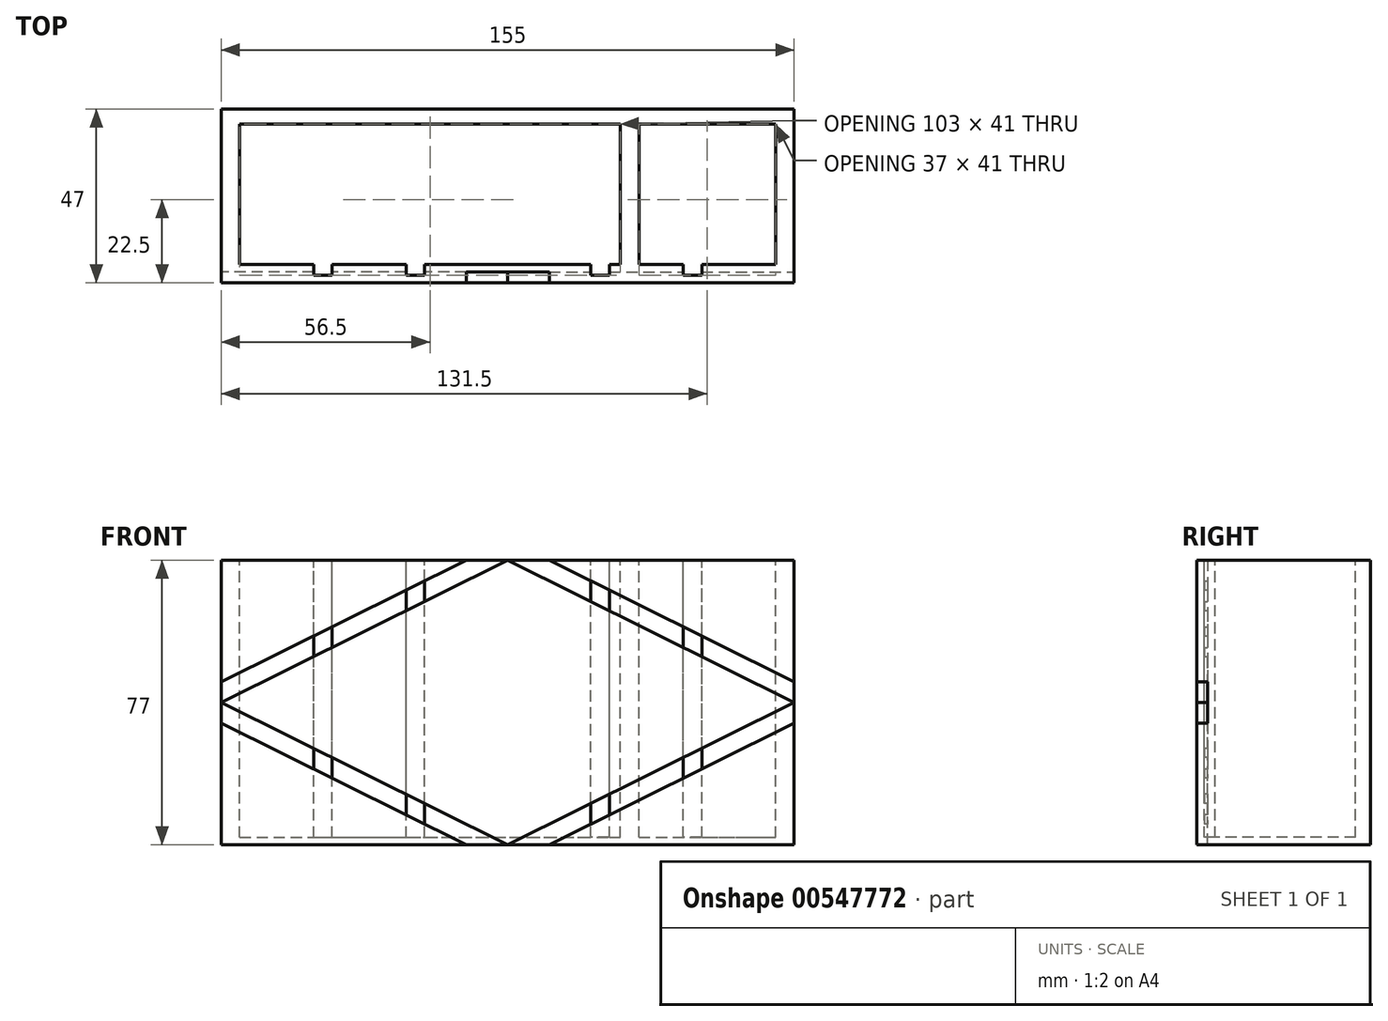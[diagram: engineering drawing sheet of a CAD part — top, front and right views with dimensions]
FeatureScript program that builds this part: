
annotation { "Feature Type Name" : "Feature", "Feature Type Description" : "" }
export const myFeature = defineFeature(function(context is Context, id is Id, definition is map)
    precondition{}
    {
        {
            var Q0;
            Q0=qCreatedBy(makeId("Top.planeOp"),FACE);
            var sketch = newSketch(context, id + "F0", { "sketchPlane" : qUnion([Q0])});
            skLineSegment(sketch, "E0.bottom", {"start": v(-77.5, 23.5) * mm, "end": v(77.5, 23.5) * mm});
            skLineSegment(sketch, "E0.top", {"start": v(-77.5, -23.5) * mm, "end": v(77.5, -23.5) * mm});
            skLineSegment(sketch, "E0.left", {"start": v(-77.5, 23.5) * mm, "end": v(-77.5, -23.5) * mm});
            skLineSegment(sketch, "E0.right", {"start": v(77.5, 23.5) * mm, "end": v(77.5, -23.5) * mm});
            skLineSegment(sketch, "E1", {"start": v(-77.5, 23.5) * mm, "end": v(77.5, -23.5) * mm, "construction": true});
            skSolve(sketch);
        }
        {
            var Q0;
            Q0=makeQuery(id+"F0.imprint","IMPRINT",FACE,{"disambiguationData":[TD([[makeQuery(id+"F0.imprint","IMPRINT",EDGE,{"derivedFrom":sQuery(id+"F0.wireOp",EDGE,"E0.bottom")}),-1.0]])]});
            extrude(context, id + "F1", {"entities" : qUnion([Q0]), "depth" : 77 * mm, "offsetDistance" : 25.4 * mm});
        }
        {
            var Q0;
            Q0=makeQuery(id+"F1.opExtrude","CAP_FACE",FACE,{"disambiguationData":[OSD([sQuery(id+"F0.wireOp",EDGE,"E0.bottom"),sQuery(id+"F0.wireOp",EDGE,"E0.top"),sQuery(id+"F0.wireOp",EDGE,"E0.left"),sQuery(id+"F0.wireOp",EDGE,"E0.right")])],"isStart":false});
            var sketch = newSketch(context, id + "F2", { "sketchPlane" : qUnion([Q0])});
            skLineSegment(sketch, "E2.bottom", {"start": v(-72.5, 19.5) * mm, "end": v(30.5, 19.5) * mm});
            skLineSegment(sketch, "E2.top", {"start": v(-72.5, -18.5) * mm, "end": v(30.5, -18.5) * mm});
            skLineSegment(sketch, "E2.left", {"start": v(-72.5, 19.5) * mm, "end": v(-72.5, -18.5) * mm});
            skLineSegment(sketch, "E2.right", {"start": v(30.5, 19.5) * mm, "end": v(30.5, -18.5) * mm});
            skLineSegment(sketch, "E3.bottom", {"start": v(35.5, 19.5) * mm, "end": v(72.5, 19.5) * mm});
            skLineSegment(sketch, "E3.top", {"start": v(35.5, -18.5) * mm, "end": v(72.5, -18.5) * mm});
            skLineSegment(sketch, "E3.left", {"start": v(35.5, 19.5) * mm, "end": v(35.5, -18.5) * mm});
            skLineSegment(sketch, "E3.right", {"start": v(72.5, 19.5) * mm, "end": v(72.5, -18.5) * mm});
            skSolve(sketch);
        }
        {
            var Q0;
            Q0=makeQuery(id+"F2.imprint","IMPRINT",FACE,{"disambiguationData":[TD([[makeQuery(id+"F2.imprint","IMPRINT",EDGE,{"derivedFrom":sQuery(id+"F2.wireOp",EDGE,"E2.bottom")}),-1.0]])]});
            var Q1;
            Q1=makeQuery(id+"F2.imprint","IMPRINT",FACE,{"disambiguationData":[TD([[makeQuery(id+"F2.imprint","IMPRINT",EDGE,{"derivedFrom":sQuery(id+"F2.wireOp",EDGE,"E3.bottom")}),-1.0]])]});
            extrude(context, id + "F3", {"entities" : qUnion([Q0, Q1]), "operationType" : NewBodyOperationType.REMOVE, "oppositeDirection" : true, "depth" : 75 * mm, "offsetDistance" : 25.4 * mm});
        }
        {
            var Q0;
            Q0=makeQuery(id+"F1.opExtrude","SWEPT_FACE",FACE,{"disambiguationData":[OSD([sQuery(id+"F0.wireOp",EDGE,"E0.top")])]});
            var sketch = newSketch(context, id + "F4", { "sketchPlane" : qUnion([Q0])});
            skLineSegment(sketch, "E4", {"start": v(0, 77) * mm, "end": v(77.5, 38.5) * mm});
            skLineSegment(sketch, "E5", {"start": v(77.5, 38.5) * mm, "end": v(0, 0) * mm});
            skLineSegment(sketch, "E6", {"start": v(0, 0) * mm, "end": v(-77.5, 38.5) * mm});
            skLineSegment(sketch, "E7", {"start": v(-77.5, 38.5) * mm, "end": v(0, 77) * mm});
            skLineSegment(sketch, "E8.0", {"start": v(-88.74, 38.5) * mm, "end": v(0, 82.58) * mm});
            skLineSegment(sketch, "E8.1", {"start": v(0, -5.58) * mm, "end": v(-88.74, 38.5) * mm});
            skLineSegment(sketch, "E8.2", {"start": v(88.74, 38.5) * mm, "end": v(0, -5.58) * mm});
            skLineSegment(sketch, "E8.3", {"start": v(0, 82.58) * mm, "end": v(88.74, 38.5) * mm});
            skSolve(sketch);
        }
        {
            var Q0;
            {var subQ0=sQuery(id+"F4.wireOp",EDGE,"E7");Q0=makeQuery(id+"F4.imprint","IMPRINT",FACE,{"disambiguationData":[TD([[makeQuery(id+"F4.imprint","IMPRINT",EDGE,{"derivedFrom":subQ0}),1.0]])]});}
            var Q1;
            {var subQ0=sQuery(id+"F4.wireOp",EDGE,"E6");Q1=makeQuery(id+"F4.imprint","IMPRINT",FACE,{"disambiguationData":[TD([[makeQuery(id+"F4.imprint","IMPRINT",EDGE,{"derivedFrom":subQ0}),1.0]])]});}
            var Q2;
            {var subQ0=sQuery(id+"F4.wireOp",EDGE,"E5");Q2=makeQuery(id+"F4.imprint","IMPRINT",FACE,{"disambiguationData":[TD([[makeQuery(id+"F4.imprint","IMPRINT",EDGE,{"derivedFrom":subQ0}),1.0]])]});}
            var Q3;
            {var subQ0=sQuery(id+"F4.wireOp",EDGE,"E4");Q3=makeQuery(id+"F4.imprint","IMPRINT",FACE,{"disambiguationData":[TD([[makeQuery(id+"F4.imprint","IMPRINT",EDGE,{"derivedFrom":subQ0}),1.0]])]});}
            extrude(context, id + "F5", {"entities" : qUnion([Q0, Q1, Q2, Q3]), "operationType" : NewBodyOperationType.REMOVE, "oppositeDirection" : true, "depth" : 3 * mm, "offsetDistance" : 25.4 * mm});
        }
        {
            var Q0;
            Q0=makeQuery(id+"F2.imprint","IMPRINT",FACE,{"disambiguationData":[TD([[makeQuery(id+"F2.imprint","IMPRINT",EDGE,{"derivedFrom":sQuery(id+"F2.wireOp",EDGE,"E2.bottom")}),1.0]])]});
            var sketch = newSketch(context, id + "F6", { "sketchPlane" : qUnion([Q0])});
            skLineSegment(sketch, "E9.bottom", {"start": v(-52.5, -18.5) * mm, "end": v(-47.5, -18.5) * mm});
            skLineSegment(sketch, "E9.top", {"start": v(-52.5, -21.5) * mm, "end": v(-47.5, -21.5) * mm});
            skLineSegment(sketch, "E9.left", {"start": v(-52.5, -18.5) * mm, "end": v(-52.5, -21.5) * mm});
            skLineSegment(sketch, "E9.right", {"start": v(-47.5, -18.5) * mm, "end": v(-47.5, -21.5) * mm});
            skLineSegment(sketch, "E10.bottom", {"start": v(-27.5, -18.5) * mm, "end": v(-22.5, -18.5) * mm});
            skLineSegment(sketch, "E10.top", {"start": v(-27.5, -21.5) * mm, "end": v(-22.5, -21.5) * mm});
            skLineSegment(sketch, "E10.left", {"start": v(-27.5, -18.5) * mm, "end": v(-27.5, -21.5) * mm});
            skLineSegment(sketch, "E10.right", {"start": v(-22.5, -18.5) * mm, "end": v(-22.5, -21.5) * mm});
            skLineSegment(sketch, "E11.bottom", {"start": v(52.5, -18.5) * mm, "end": v(47.5, -18.5) * mm});
            skLineSegment(sketch, "E11.top", {"start": v(52.5, -21.5) * mm, "end": v(47.5, -21.5) * mm});
            skLineSegment(sketch, "E11.left", {"start": v(52.5, -18.5) * mm, "end": v(52.5, -21.5) * mm});
            skLineSegment(sketch, "E11.right", {"start": v(47.5, -18.5) * mm, "end": v(47.5, -21.5) * mm});
            skLineSegment(sketch, "E12.bottom", {"start": v(27.5, -18.5) * mm, "end": v(22.5, -18.5) * mm});
            skLineSegment(sketch, "E12.top", {"start": v(27.5, -21.5) * mm, "end": v(22.5, -21.5) * mm});
            skLineSegment(sketch, "E12.left", {"start": v(27.5, -18.5) * mm, "end": v(27.5, -21.5) * mm});
            skLineSegment(sketch, "E12.right", {"start": v(22.5, -18.5) * mm, "end": v(22.5, -21.5) * mm});
            skSolve(sketch);
        }
        {
            var Q0;
            Q0=makeQuery(id+"F6.imprint","IMPRINT",FACE,{"disambiguationData":[TD([[makeQuery(id+"F6.imprint","IMPRINT",EDGE,{"derivedFrom":sQuery(id+"F6.wireOp",EDGE,"E11.bottom")}),-1.0]])]});
            var Q1;
            Q1=makeQuery(id+"F6.imprint","IMPRINT",FACE,{"disambiguationData":[TD([[makeQuery(id+"F6.imprint","IMPRINT",EDGE,{"derivedFrom":sQuery(id+"F6.wireOp",EDGE,"E12.bottom")}),-1.0]])]});
            var Q2;
            Q2=makeQuery(id+"F6.imprint","IMPRINT",FACE,{"disambiguationData":[TD([[makeQuery(id+"F6.imprint","IMPRINT",EDGE,{"derivedFrom":sQuery(id+"F6.wireOp",EDGE,"E10.bottom")}),-1.0]])]});
            var Q3;
            Q3=makeQuery(id+"F6.imprint","IMPRINT",FACE,{"disambiguationData":[TD([[makeQuery(id+"F6.imprint","IMPRINT",EDGE,{"derivedFrom":sQuery(id+"F6.wireOp",EDGE,"E9.bottom")}),-1.0]])]});
            extrude(context, id + "F7", {"entities" : qUnion([Q0, Q1, Q2, Q3]), "operationType" : NewBodyOperationType.REMOVE, "oppositeDirection" : true, "depth" : 75 * mm, "offsetDistance" : 25.4 * mm});
        }
    });
